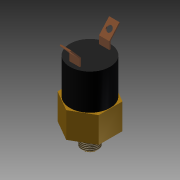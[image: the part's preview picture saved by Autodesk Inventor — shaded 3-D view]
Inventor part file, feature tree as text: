
AUTODESK INVENTOR PART (.ipt)
format: ipt  version: 2011 (Build 150239000, 239)  size: 150,016 bytes
history: native  units: mm (DEFAULTED — no unit token found)
features: extrude x6, sketch x6, projected_geometry x4, mirror x1, thread x1, chamfer x1, fillet x1
ambient origin geometry x8: Origin, YZ Plane, XZ Plane, XY Plane, X Axis, Y Axis, Z Axis, Center Point
bodies: Solid1 (feature_tree)
feature tree (20):
  extrude  "Extrusion1"  Depth=15.875mm TaperAngle=0.0deg
  extrude  "Extrusion2"  Depth=11.049mm TaperAngle=0.0deg
  extrude  "Extrusion3"  Depth=19.9898mm TaperAngle=0.0deg
  extrude  "Extrusion4"  Depth=21.971mm TaperAngle=0.0deg
  extrude  "Extrusion5"  Depth=0.762mm
  extrude  "Extrusion6"  Depth=4.699mm
  mirror  "Mirror1"
  thread  "Thread1"  [1 undecoded]
  chamfer  "Chamfer1"  Distance=6.35mm
  fillet  "Fillet1"  Radius=6.35mm
  sketch  "Sketch1"  dims[d0=25.4mm d1=15.875mm d2=0.0mm]
  sketch  "Sketch2"  dims[d3=10.16mm d4=11.049mm d5=0.0mm]
  projected_geometry  "Projected Loop1"
  sketch  "Sketch3"  dims[d6=3.175mm d7=19.9898mm d8=0.0mm]
  sketch  "Sketch4"  dims[d9=24.765mm d10=21.971mm d11=0.0mm]
  projected_geometry  "Projected Loop2"
  sketch  "Sketch5"  dims[d12=19.05mm d13=0.762mm]
  projected_geometry  "Projected Loop3"
  sketch  "Sketch6"  dims[d14=0.762mm d15=4.699mm d17=9.398mm d18=6.35mm d19=0.0mm d20=6.35mm d21=0.0mm d22=25.4mm d23=0.0mm d24=1.0mm d25=3.175mm d26=45.0deg d27=3.175mm]
  projected_geometry  "Projected Loop4"
note: 1 required parameter value undecoded (feature->parameter linkage not recoverable at this tier; creation-order binding heuristic only, values carry confidence <= 0.55)
